# Revit family: rba-bim-rba8140-500
name_source: partatom
category: Specialty Equipment
revit_build: Autodesk Revit 2018 (Build: 20170223_1515(x64)
units: mm (PartAtom-declared; Revit-internal decimal feet)

## family parameters
Cut with Voids When Loaded = No
Host = Face
OmniClass Number = 23.40.20.21.17
OmniClass Title = Paper Towel Dispensers, Disposal Units
Part Type = Normal
Room Calculation Point = No
Round Connector Dimension = Use Diameter
Shared = Yes

## types (1)
- RBA8140-500
    -OCC Optional Corterra Color Specify OCC- = No
    Assembly Code = C1030200
    Default Elevation = 0 mm  [stored 0 ft]
    Description = Recessed Dignity Ligature Resistant Toilet Roll Holder
    Frame Height = 254 mm
    Frame Length = 152 mm
    Frame Thickness = 86 mm
    Height = 292 mm
    Holder Material = Polymer Resin Corterra-Whitehall-Blanco (OCC11)
    Installation Type = Wall Mounted
    Length = 178 mm
    Manufacturer = RBA Group
    Materials and Finishes = Corterra® Solid Surface
    Model = RBA8140-500
    Modified Issue = 20211020.01
    Mounting Frame Material = Metal-Whitehall-Galvanized Steel
    Price = Prices may vary. Please consult Manufacturer Representative for most up-to-date price list.
    Product Documentation Link = https://www.whitehallmfg.com
    URL = www.rba.com.au
    Warranty Documentation Link = https://www.whitehallmfg.com

note: [stored X ft] marks values corroborated as IEEE doubles in the binary element streams (Revit-internal decimal feet)

## geometry (parser evidence)
native form markers: Sweep x3
no freeform markers — native parametric forms only
